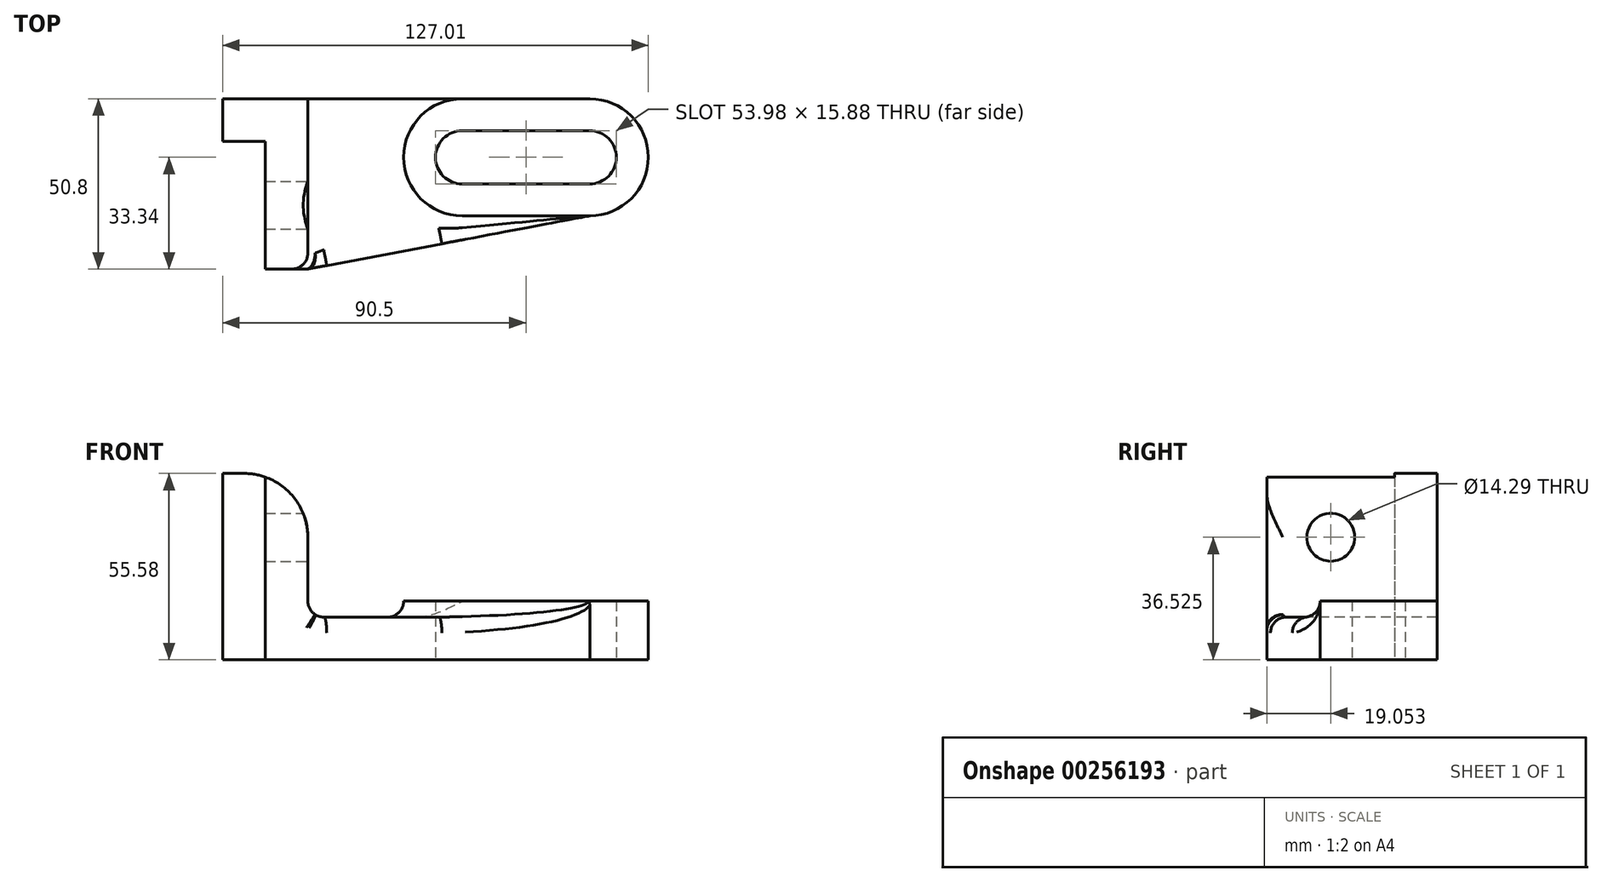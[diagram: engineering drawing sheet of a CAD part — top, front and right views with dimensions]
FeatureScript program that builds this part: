
annotation { "Feature Type Name" : "Feature", "Feature Type Description" : "" }
export const myFeature = defineFeature(function(context is Context, id is Id, definition is map)
    precondition{}
    {
        {
            var Q0;
            Q0=qCreatedBy(makeId("Top.planeOp"),FACE);
            var sketch = newSketch(context, id + "F0", { "sketchPlane" : qUnion([Q0])});
            skArc(sketch, "E0", {"start": v(0, 7.94) * mm, "mid": v(-7.94, 0) * mm, "end": v(0, -7.94) * mm});
            skArc(sketch, "E1", {"start": v(38.1, -7.94) * mm, "mid": v(46.04, 0) * mm, "end": v(38.1, 7.94) * mm});
            skLineSegment(sketch, "E2", {"start": v(0, 7.94) * mm, "end": v(38.1, 7.94) * mm});
            skLineSegment(sketch, "E3", {"start": v(0, -7.94) * mm, "end": v(38.1, -7.94) * mm});
            skArc(sketch, "E4", {"start": v(0, 17.46) * mm, "mid": v(-17.46, 0) * mm, "end": v(0, -17.46) * mm});
            skArc(sketch, "E5", {"start": v(38.1, -17.46) * mm, "mid": v(55.56, 0) * mm, "end": v(38.1, 17.46) * mm});
            skLineSegment(sketch, "E6", {"start": v(0, 17.46) * mm, "end": v(38.1, 17.46) * mm});
            skLineSegment(sketch, "E7", {"start": v(0, -17.46) * mm, "end": v(38.1, -17.46) * mm});
            skPoint(sketch, "E8", {"position": v(38.1, -17.46) * mm});
            skLineSegment(sketch, "E9", {"start": v(0, 17.46) * mm, "end": v(-71.45, 17.46) * mm});
            skLineSegment(sketch, "E10", {"start": v(-71.45, 17.46) * mm, "end": v(-71.45, 4.76) * mm});
            skLineSegment(sketch, "E11", {"start": v(-71.45, 4.76) * mm, "end": v(-58.75, 4.76) * mm});
            skLineSegment(sketch, "E12", {"start": v(-58.75, 4.76) * mm, "end": v(-58.75, -33.34) * mm});
            skLineSegment(sketch, "E13", {"start": v(-58.75, -33.34) * mm, "end": v(-46.05, -33.34) * mm});
            skLineSegment(sketch, "E14", {"start": v(-46.05, -33.34) * mm, "end": v(-46.05, 17.46) * mm});
            skLineSegment(sketch, "E15", {"start": v(-46.05, -33.34) * mm, "end": v(38.1, -17.46) * mm});
            skSolve(sketch);
        }
        {
            var Q0;
            {var subQ0=sQuery(id+"F0.wireOp",EDGE,"E10");Q0=makeQuery(id+"F0.imprint","IMPRINT",FACE,{"disambiguationData":[TD([[makeQuery(id+"F0.imprint","IMPRINT",EDGE,{"derivedFrom":subQ0}),1.0]])]});}
            var Q1;
            {var subQ2=sQuery(id+"F0.wireOp",EDGE,"E4");Q1=makeQuery(id+"F0.imprint","IMPRINT",FACE,{"disambiguationData":[TD([[makeQuery(id+"F0.imprint","IMPRINT",EDGE,{"derivedFrom":subQ2}),-1.0]])]});}
            var Q2;
            Q2=makeQuery(id+"F0.imprint","IMPRINT",FACE,{"disambiguationData":[TD([[makeQuery(id+"F0.imprint","IMPRINT",EDGE,{"derivedFrom":sQuery(id+"F0.wireOp",EDGE,"E0")}),-1.0]])]});
            extrude(context, id + "F1", {"entities" : qUnion([Q0, Q1, Q2]), "depth" : 12.7 * mm});
        }
        {
            var Q0;
            Q0=makeQuery(id+"F0.imprint","IMPRINT",FACE,{"disambiguationData":[TD([[makeQuery(id+"F0.imprint","IMPRINT",EDGE,{"derivedFrom":sQuery(id+"F0.wireOp",EDGE,"E0")}),-1.0]])]});
            extrude(context, id + "F2", {"entities" : qUnion([Q0]), "operationType" : NewBodyOperationType.ADD, "depth" : 17.48 * mm});
        }
        {
            var Q0;
            {var subQ0=sQuery(id+"F0.wireOp",EDGE,"E10");Q0=makeQuery(id+"F0.imprint","IMPRINT",FACE,{"disambiguationData":[TD([[makeQuery(id+"F0.imprint","IMPRINT",EDGE,{"derivedFrom":subQ0}),1.0]])]});}
            extrude(context, id + "F3", {"entities" : qUnion([Q0]), "operationType" : NewBodyOperationType.ADD, "depth" : 55.58 * mm});
        }
        {
            var Q0;
            Q0=makeQuery(id+"F3.boolean.opBoolean","INTERSECT",EDGE,{"derivedFrom":[makeQuery(id+"F1.opExtrude","CAP_FACE",FACE,{"disambiguationData":[OSD([sQuery(id+"F0.wireOp",EDGE,"E0"),sQuery(id+"F0.wireOp",EDGE,"E1"),sQuery(id+"F0.wireOp",EDGE,"E2"),sQuery(id+"F0.wireOp",EDGE,"E3"),sQuery(id+"F0.wireOp",EDGE,"E5"),sQuery(id+"F0.wireOp",EDGE,"E6"),sQuery(id+"F0.wireOp",EDGE,"E9"),sQuery(id+"F0.wireOp",EDGE,"E10"),sQuery(id+"F0.wireOp",EDGE,"E11"),sQuery(id+"F0.wireOp",EDGE,"E12"),sQuery(id+"F0.wireOp",EDGE,"E13"),sQuery(id+"F0.wireOp",EDGE,"E15")])],"isStart":false}),makeQuery(id+"F3.opExtrude","SWEPT_FACE",FACE,{"disambiguationData":[OSD([sQuery(id+"F0.wireOp",EDGE,"E14")])]})]});
            fillet(context, id + "F4", {"entities" : qUnion([Q0]), "radius" : 4.76 * mm, "tangentPropagation" : true, "allowEdgeOverflow" : false});
        }
        {
            var Q0;
            Q0=makeQuery(id+"F2.boolean.opBoolean","INTERSECT",EDGE,{"derivedFrom":[makeQuery(id+"F1.opExtrude","CAP_FACE",FACE,{"disambiguationData":[OSD([sQuery(id+"F0.wireOp",EDGE,"E0"),sQuery(id+"F0.wireOp",EDGE,"E1"),sQuery(id+"F0.wireOp",EDGE,"E2"),sQuery(id+"F0.wireOp",EDGE,"E3"),sQuery(id+"F0.wireOp",EDGE,"E5"),sQuery(id+"F0.wireOp",EDGE,"E6"),sQuery(id+"F0.wireOp",EDGE,"E9"),sQuery(id+"F0.wireOp",EDGE,"E10"),sQuery(id+"F0.wireOp",EDGE,"E11"),sQuery(id+"F0.wireOp",EDGE,"E12"),sQuery(id+"F0.wireOp",EDGE,"E13"),sQuery(id+"F0.wireOp",EDGE,"E15")])],"isStart":false}),makeQuery(id+"F2.opExtrude","SWEPT_FACE",FACE,{"disambiguationData":[OSD([sQuery(id+"F0.wireOp",EDGE,"E4")])]})]});
            var Q1;
            Q1=makeQuery(id+"F2.boolean.opBoolean","INTERSECT",EDGE,{"derivedFrom":[makeQuery(id+"F1.opExtrude","CAP_FACE",FACE,{"disambiguationData":[OSD([sQuery(id+"F0.wireOp",EDGE,"E0"),sQuery(id+"F0.wireOp",EDGE,"E1"),sQuery(id+"F0.wireOp",EDGE,"E2"),sQuery(id+"F0.wireOp",EDGE,"E3"),sQuery(id+"F0.wireOp",EDGE,"E5"),sQuery(id+"F0.wireOp",EDGE,"E6"),sQuery(id+"F0.wireOp",EDGE,"E9"),sQuery(id+"F0.wireOp",EDGE,"E10"),sQuery(id+"F0.wireOp",EDGE,"E11"),sQuery(id+"F0.wireOp",EDGE,"E12"),sQuery(id+"F0.wireOp",EDGE,"E13"),sQuery(id+"F0.wireOp",EDGE,"E15")])],"isStart":false}),makeQuery(id+"F2.opExtrude","SWEPT_FACE",FACE,{"disambiguationData":[OSD([sQuery(id+"F0.wireOp",EDGE,"E7")])]})]});
            fillet(context, id + "F5", {"entities" : qUnion([Q0, Q1]), "radius" : 4.76 * mm, "tangentPropagation" : true, "allowEdgeOverflow" : false});
        }
        {
            var Q0;
            Q0=makeQuery(id+"F1.opExtrude","CAP_EDGE",EDGE,{"disambiguationData":[OSD([sQuery(id+"F0.wireOp",EDGE,"E15")])],"isStart":false});
            var Q1;
            {var subQ0=sQuery(id+"F0.wireOp",EDGE,"E15");Q1=makeQuery(id+"F5.opFillet","BLEND_EDGE",EDGE,{"blendedFrom":[makeQuery(id+"F2.boolean.opBoolean","INTERSECT",EDGE,{"derivedFrom":[makeQuery(id+"F1.opExtrude","CAP_FACE",FACE,{"disambiguationData":[OSD([sQuery(id+"F0.wireOp",EDGE,"E0"),sQuery(id+"F0.wireOp",EDGE,"E1"),sQuery(id+"F0.wireOp",EDGE,"E2"),sQuery(id+"F0.wireOp",EDGE,"E3"),sQuery(id+"F0.wireOp",EDGE,"E5"),sQuery(id+"F0.wireOp",EDGE,"E6"),sQuery(id+"F0.wireOp",EDGE,"E9"),sQuery(id+"F0.wireOp",EDGE,"E10"),sQuery(id+"F0.wireOp",EDGE,"E11"),sQuery(id+"F0.wireOp",EDGE,"E12"),sQuery(id+"F0.wireOp",EDGE,"E13"),subQ0])],"isStart":false}),makeQuery(id+"F2.opExtrude","SWEPT_FACE",FACE,{"disambiguationData":[OSD([sQuery(id+"F0.wireOp",EDGE,"E7")])]})]}),makeQuery(id+"F1.opExtrude","SWEPT_FACE",FACE,{"disambiguationData":[OSD([subQ0])]})],"blendedInto":[makeQuery(id+"F1.opExtrude","SWEPT_FACE",FACE,{"disambiguationData":[OSD([subQ0])]})]});}
            fillet(context, id + "F6", {"entities" : qUnion([Q0, Q1]), "radius" : 4.76 * mm, "tangentPropagation" : true, "allowEdgeOverflow" : false});
        }
        {
            var Q0;
            Q0=makeQuery(id+"F3.opExtrude","SWEPT_FACE",FACE,{"disambiguationData":[OSD([sQuery(id+"F0.wireOp",EDGE,"E14")])]});
            var sketch = newSketch(context, id + "F7", { "sketchPlane" : qUnion([Q0])});
            skCircle(sketch, "E16", {"center": v(-14.29, 36.53) * mm, "radius": 7.14 * mm});
            skLineSegment(sketch, "E17", {"start": v(-14.29, 36.53) * mm, "end": v(-14.29, 55.58) * mm, "construction": true});
            skLineSegment(sketch, "E18", {"start": v(-14.29, 36.53) * mm, "end": v(-33.34, 36.53) * mm, "construction": true});
            skSolve(sketch);
        }
        {
            var Q0;
            Q0=sQuery(id+"F7.wireOp",VERTEX,"E17.start");
            var Q1;
            Q1=makeQuery(id+"F1.opExtrude","SWEPT_BODY",BODY,{"disambiguationData":[OSD([sQuery(id+"F0.wireOp",EDGE,"E0"),sQuery(id+"F0.wireOp",EDGE,"E1"),sQuery(id+"F0.wireOp",EDGE,"E2"),sQuery(id+"F0.wireOp",EDGE,"E3"),sQuery(id+"F0.wireOp",EDGE,"E5"),sQuery(id+"F0.wireOp",EDGE,"E6"),sQuery(id+"F0.wireOp",EDGE,"E9"),sQuery(id+"F0.wireOp",EDGE,"E10"),sQuery(id+"F0.wireOp",EDGE,"E11"),sQuery(id+"F0.wireOp",EDGE,"E12"),sQuery(id+"F0.wireOp",EDGE,"E13"),sQuery(id+"F0.wireOp",EDGE,"E15")])]});
            hole(context, id + "F8", {"style" : HoleStyle.SIMPLE, "endStyle" : HoleEndStyle.THROUGH, "holeDiameter" : 14.29 * mm, "tappedDepth" : 12.7 * mm, "tapClearance" : 3, "locations" : qUnion([Q0]), "scope" : qUnion([Q1])});
        }
        {
            var Q0;
            Q0=makeQuery(id+"F3.opExtrude","CAP_EDGE",EDGE,{"disambiguationData":[OSD([sQuery(id+"F0.wireOp",EDGE,"E13")])],"isStart":false});
            fillet(context, id + "F9", {"entities" : qUnion([Q0]), "radius" : 19.05 * mm, "tangentPropagation" : true, "allowEdgeOverflow" : false});
        }
        {
            var Q0;
            Q0=makeQuery(id+"F3.opExtrude","CAP_EDGE",EDGE,{"disambiguationData":[OSD([sQuery(id+"F0.wireOp",EDGE,"E14")])],"isStart":false});
            var Q1;
            Q1=makeQuery(id+"F1.opExtrude","SWEPT_EDGE",EDGE,{"disambiguationData":[OSD([sQuery(id+"F0.wireOp",EDGE,"E13"),sQuery(id+"F0.wireOp",EDGE,"E14"),sQuery(id+"F0.wireOp",EDGE,"E15")])]});
            fillet(context, id + "F10", {"entities" : qUnion([Q0, Q1]), "radius" : 4.76 * mm, "tangentPropagation" : true, "allowEdgeOverflow" : false});
        }
    });
